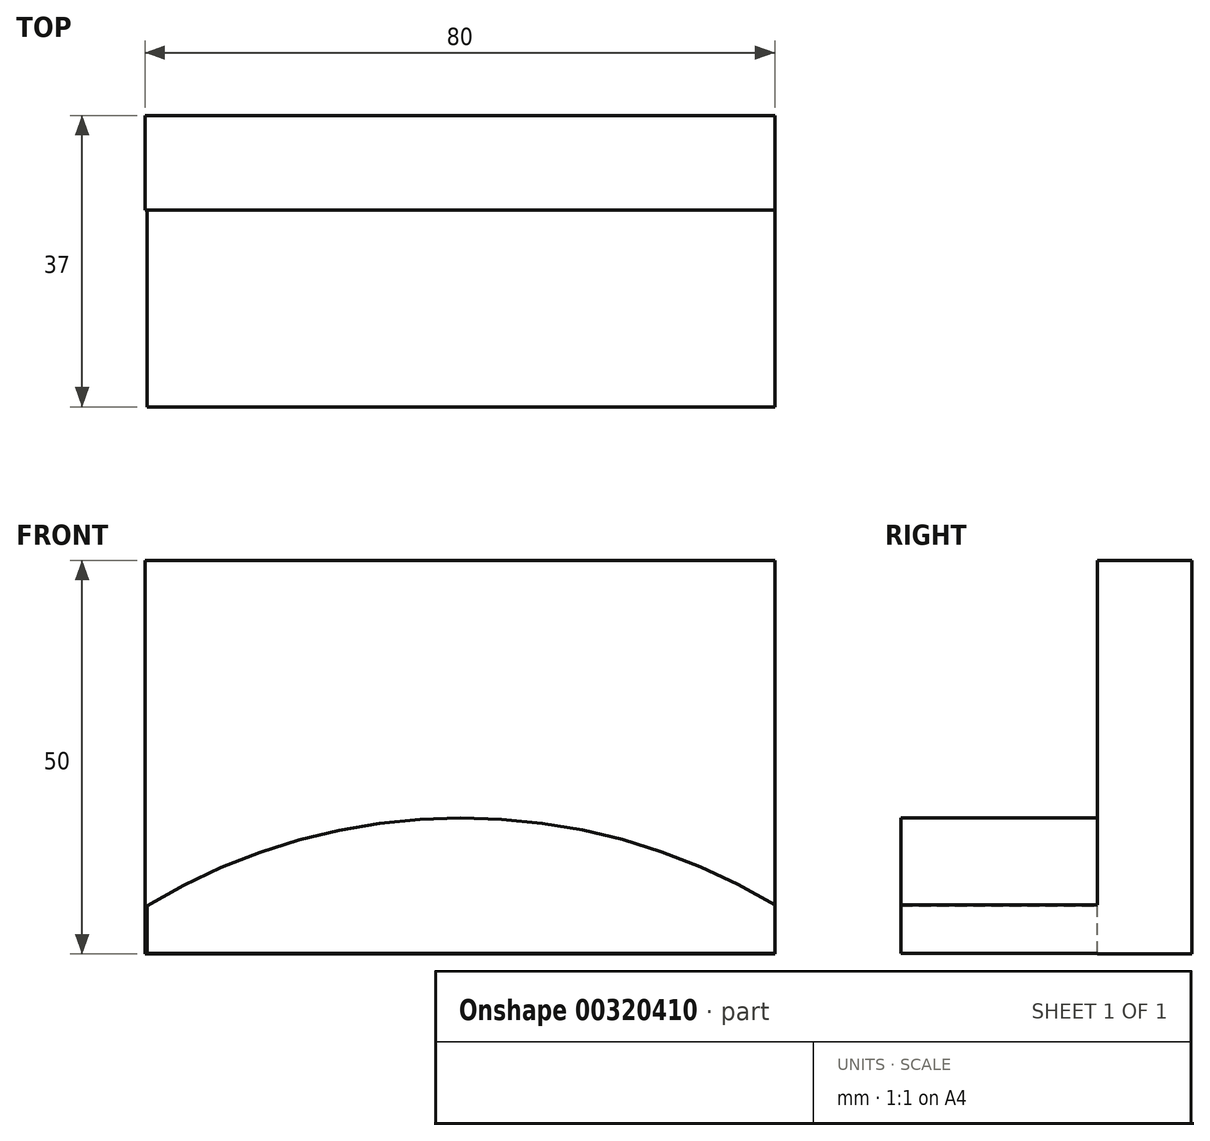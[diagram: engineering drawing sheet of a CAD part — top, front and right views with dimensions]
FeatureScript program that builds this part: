
annotation { "Feature Type Name" : "Feature", "Feature Type Description" : "" }
export const myFeature = defineFeature(function(context is Context, id is Id, definition is map)
    precondition{}
    {
        {
            var Q0;
            Q0=qCreatedBy(makeId("Front.planeOp"),FACE);
            var sketch = newSketch(context, id + "F0", { "sketchPlane" : qUnion([Q0])});
            skLineSegment(sketch, "E0.bottom", {"start": v(0, 50) * mm, "end": v(80, 50) * mm});
            skLineSegment(sketch, "E0.top", {"start": v(0, 0) * mm, "end": v(80, 0) * mm});
            skLineSegment(sketch, "E0.left", {"start": v(0, 50) * mm, "end": v(0, 0) * mm});
            skLineSegment(sketch, "E0.right", {"start": v(80, 50) * mm, "end": v(80, 0) * mm});
            skSolve(sketch);
        }
        {
            var Q0;
            Q0 = qSketchRegion(id + "F0", true);
            extrude(context, id + "F1", {"entities" : qUnion([Q0]), "endBound" : BoundingType.SYMMETRIC, "depth" : 12 * mm});
        }
        {
            var Q0;
            Q0=makeQuery(id+"F1.opExtrude","CAP_FACE",FACE,{"disambiguationData":[OSD([sQuery(id+"F0.wireOp",EDGE,"E0.bottom"),sQuery(id+"F0.wireOp",EDGE,"E0.top"),sQuery(id+"F0.wireOp",EDGE,"E0.left"),sQuery(id+"F0.wireOp",EDGE,"E0.right")])],"isStart":false});
            var sketch = newSketch(context, id + "F2", { "sketchPlane" : qUnion([Q0])});
            skArc(sketch, "E1", {"start": v(0.23, 6.1) * mm, "mid": v(40.23, 17.27) * mm, "end": v(80.23, 6.1) * mm});
            skPoint(sketch, "E2.orphan", {"position": v(0.23, -2.46) * mm});
            skPoint(sketch, "E3.orphan", {"position": v(0.23, 6.1) * mm});
            skLineSegment(sketch, "E4.0", {"start": v(0.23, 0.1) * mm, "end": v(80.23, 0.1) * mm});
            skLineSegment(sketch, "E5", {"start": v(0.23, 0.1) * mm, "end": v(0.23, 6.1) * mm});
            skLineSegment(sketch, "E6", {"start": v(80.23, 0.1) * mm, "end": v(80.23, 6.1) * mm});
            skSolve(sketch);
        }
        {
            var Q0;
            {var subQ0=sQuery(id+"F2.wireOp",EDGE,"E5");Q0=makeQuery(id+"F2.imprint","IMPRINT",FACE,{"disambiguationData":[TD([[makeQuery(id+"F2.imprint","IMPRINT",EDGE,{"derivedFrom":subQ0}),-1.0]])]});}
            extrude(context, id + "F3", {"entities" : qUnion([Q0]), "operationType" : NewBodyOperationType.ADD, "depth" : 25 * mm});
        }
    });
